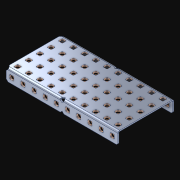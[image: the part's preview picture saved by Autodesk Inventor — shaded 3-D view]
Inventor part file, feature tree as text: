
AUTODESK INVENTOR PART (.ipt)
format: ipt  version: 2021 (Build 250183000, 183)  size: 1,649,664 bytes
history: native  units: in
note: dims shown in document units (in); Inventor stores cm internally (conversion verified against a paired STEP export)
features: extrude x71, other x71, sketch x4, pattern_linear x3
ambient origin geometry x8: Origin, YZ Plane, XZ Plane, XY Plane, X Axis, Y Axis, Z Axis, Center Point
bodies: Solid1 (feature_tree)
feature tree (149):
  pattern_linear  "Rectangular Pattern1"  Spacing1=0.182in  [1 undecoded]
  pattern_linear  "Rectangular Pattern2"  Spacing1=0.046in  [1 undecoded]
  pattern_linear  "Rectangular Pattern3"  Spacing1=0.5in  [1 undecoded]
  extrude  "Extrusion1"  Depth=0.046in
  sketch  "Sketch1"  dims[d0=0.182in]
  other  "Srf1"
  sketch  "Sketch2"  dims[d1=0.046in d2=0.0in]
  other  "Srf2"
  sketch  "Sketch3"  dims[d3=0.182in]
  other  "Srf3"
  other  "Srf4"
  other  "Srf5"
  other  "Srf6"
  other  "Srf7"
  other  "Srf8"
  other  "Srf9"
  other  "Srf10"
  other  "Srf11"
  other  "Srf12"
  other  "Srf38"
  other  "Srf39"
  other  "Srf40"
  other  "Srf41"
  other  "Srf42"
  other  "Srf43"
  other  "Srf44"
  other  "Srf45"
  other  "Srf46"
  other  "Srf72"
  other  "Srf73"
  other  "Srf74"
  other  "Srf75"
  other  "Srf76"
  other  "Srf77"
  other  "Srf78"
  other  "Srf79"
  other  "Srf80"
  other  "Srf81"
  other  "Srf107"
  other  "Srf108"
  other  "Srf109"
  other  "Srf110"
  other  "Srf111"
  other  "Srf112"
  other  "Srf113"
  other  "Srf114"
  other  "Srf115"
  other  "Srf116"
  other  "Srf142"
  other  "Srf143"
  other  "Srf144"
  other  "Srf145"
  other  "Srf146"
  other  "Srf147"
  other  "Srf148"
  other  "Srf149"
  other  "Srf150"
  other  "Srf151"
  other  "Srf177"
  other  "Srf178"
  other  "Srf179"
  other  "Srf180"
  other  "Srf181"
  other  "Srf182"
  other  "Srf183"
  other  "Srf184"
  other  "Srf185"
  other  "Srf186"
  other  "Srf212"
  other  "Srf213"
  other  "Srf214"
  other  "Srf215"
  other  "Srf216"
  other  "Srf217"
  other  "Srf218"
  other  "Srf219"
  other  "Srf220"
  sketch  "Sketch4"  dims[d4=0.046in d5=0.0in d6=0.182in d7=0.046in d8=0.0in d11=0.5in d12=3.937in d14=0.5in d15=1.9685in d17=0.5in d18=3.937in d20=0.5in d21=12.5in d22=0.0in]
  parser-record x1  (decoder bookkeeping rows leaked as tree rows — omitted from the tree; the rows remain in map.json)
  extrude  "ExtrusionSrf1"  Depth=0.046in
  extrude  "ExtrusionSrf2"  Depth=0.046in
  extrude  "ExtrusionSrf3"  Depth=0.046in
  extrude  "ExtrusionSrf4"  Depth=0.046in
  extrude  "ExtrusionSrf5"  Depth=0.046in
  extrude  "ExtrusionSrf6"  TaperAngle=0.0deg  [1 undecoded]
  extrude  "ExtrusionSrf7"  [1 undecoded]
  extrude  "ExtrusionSrf8"  [1 undecoded]
  extrude  "ExtrusionSrf9"  [1 undecoded]
  extrude  "ExtrusionSrf10"  [1 undecoded]
  extrude  "ExtrusionSrf11"  [1 undecoded]
  extrude  "ExtrusionSrf12"  [1 undecoded]
  extrude  "ExtrusionSrf38"  [1 undecoded]
  extrude  "ExtrusionSrf39"  [1 undecoded]
  extrude  "ExtrusionSrf40"  [1 undecoded]
  extrude  "ExtrusionSrf41"  [1 undecoded]
  extrude  "ExtrusionSrf42"  [1 undecoded]
  extrude  "ExtrusionSrf43"  [1 undecoded]
  extrude  "ExtrusionSrf44"  [1 undecoded]
  extrude  "ExtrusionSrf45"  [1 undecoded]
  extrude  "ExtrusionSrf46"  [1 undecoded]
  extrude  "ExtrusionSrf72"  [1 undecoded]
  extrude  "ExtrusionSrf73"  [1 undecoded]
  extrude  "ExtrusionSrf74"  [1 undecoded]
  extrude  "ExtrusionSrf75"  [1 undecoded]
  extrude  "ExtrusionSrf76"  [1 undecoded]
  extrude  "ExtrusionSrf77"  [1 undecoded]
  extrude  "ExtrusionSrf78"  [1 undecoded]
  extrude  "ExtrusionSrf79"  [1 undecoded]
  extrude  "ExtrusionSrf80"  [1 undecoded]
  extrude  "ExtrusionSrf81"  [1 undecoded]
  extrude  "ExtrusionSrf107"  [1 undecoded]
  extrude  "ExtrusionSrf108"  [1 undecoded]
  extrude  "ExtrusionSrf109"  [1 undecoded]
  extrude  "ExtrusionSrf110"  [1 undecoded]
  extrude  "ExtrusionSrf111"  [1 undecoded]
  extrude  "ExtrusionSrf112"  [1 undecoded]
  extrude  "ExtrusionSrf113"  [1 undecoded]
  extrude  "ExtrusionSrf114"  [1 undecoded]
  extrude  "ExtrusionSrf115"  [1 undecoded]
  extrude  "ExtrusionSrf116"  [1 undecoded]
  extrude  "ExtrusionSrf142"  [1 undecoded]
  extrude  "ExtrusionSrf143"  [1 undecoded]
  extrude  "ExtrusionSrf144"  [1 undecoded]
  extrude  "ExtrusionSrf145"  [1 undecoded]
  extrude  "ExtrusionSrf146"  [1 undecoded]
  extrude  "ExtrusionSrf147"  [1 undecoded]
  extrude  "ExtrusionSrf148"  [1 undecoded]
  extrude  "ExtrusionSrf149"  [1 undecoded]
  extrude  "ExtrusionSrf150"  [1 undecoded]
  extrude  "ExtrusionSrf151"  [1 undecoded]
  extrude  "ExtrusionSrf177"  [1 undecoded]
  extrude  "ExtrusionSrf178"  [1 undecoded]
  extrude  "ExtrusionSrf179"  [1 undecoded]
  extrude  "ExtrusionSrf180"  [1 undecoded]
  extrude  "ExtrusionSrf181"  [1 undecoded]
  extrude  "ExtrusionSrf182"  [1 undecoded]
  extrude  "ExtrusionSrf183"  [1 undecoded]
  extrude  "ExtrusionSrf184"  [1 undecoded]
  extrude  "ExtrusionSrf185"  [1 undecoded]
  extrude  "ExtrusionSrf186"  [1 undecoded]
  extrude  "ExtrusionSrf212"  [1 undecoded]
  extrude  "ExtrusionSrf213"  [1 undecoded]
  extrude  "ExtrusionSrf214"  [1 undecoded]
  extrude  "ExtrusionSrf215"  [1 undecoded]
  extrude  "ExtrusionSrf216"  [1 undecoded]
  extrude  "ExtrusionSrf217"  [1 undecoded]
  extrude  "ExtrusionSrf218"  [1 undecoded]
  extrude  "ExtrusionSrf219"  [1 undecoded]
  extrude  "ExtrusionSrf220"  [1 undecoded]
note: 68 required parameter values undecoded (feature->parameter linkage not recoverable at this tier; creation-order binding heuristic only, values carry confidence <= 0.55)
